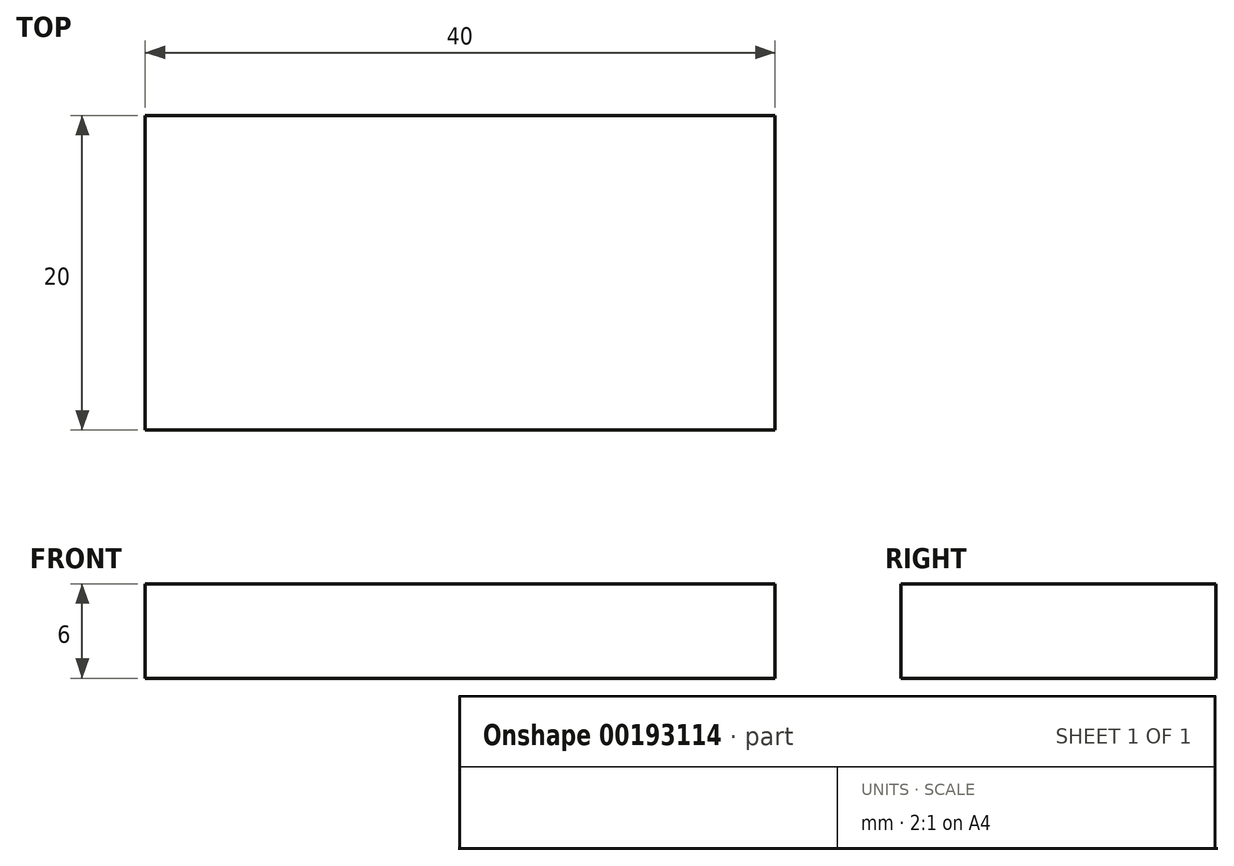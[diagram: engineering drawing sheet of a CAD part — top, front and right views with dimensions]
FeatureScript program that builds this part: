
annotation { "Feature Type Name" : "Feature", "Feature Type Description" : "" }
export const myFeature = defineFeature(function(context is Context, id is Id, definition is map)
    precondition{}
    {
        {
            var Q0;
            Q0=qCreatedBy(makeId("Top.planeOp"),FACE);
            var sketch = newSketch(context, id + "F0", { "sketchPlane" : qUnion([Q0])});
            skLineSegment(sketch, "E0.bottom", {"start": v(0, 0) * mm, "end": v(40, 0) * mm});
            skLineSegment(sketch, "E0.top", {"start": v(0, 20) * mm, "end": v(40, 20) * mm});
            skLineSegment(sketch, "E0.left", {"start": v(0, 0) * mm, "end": v(0, 20) * mm});
            skLineSegment(sketch, "E0.right", {"start": v(40, 0) * mm, "end": v(40, 20) * mm});
            skSolve(sketch);
        }
        {
            var Q0;
            Q0=makeQuery(id+"F0.imprint","IMPRINT",FACE,{"disambiguationData":[TD([[makeQuery(id+"F0.imprint","IMPRINT",EDGE,{"derivedFrom":sQuery(id+"F0.wireOp",EDGE,"E0.bottom")}),1.0]])]});
            extrude(context, id + "F1", {"entities" : qUnion([Q0]), "depth" : 6 * mm});
        }
    });
